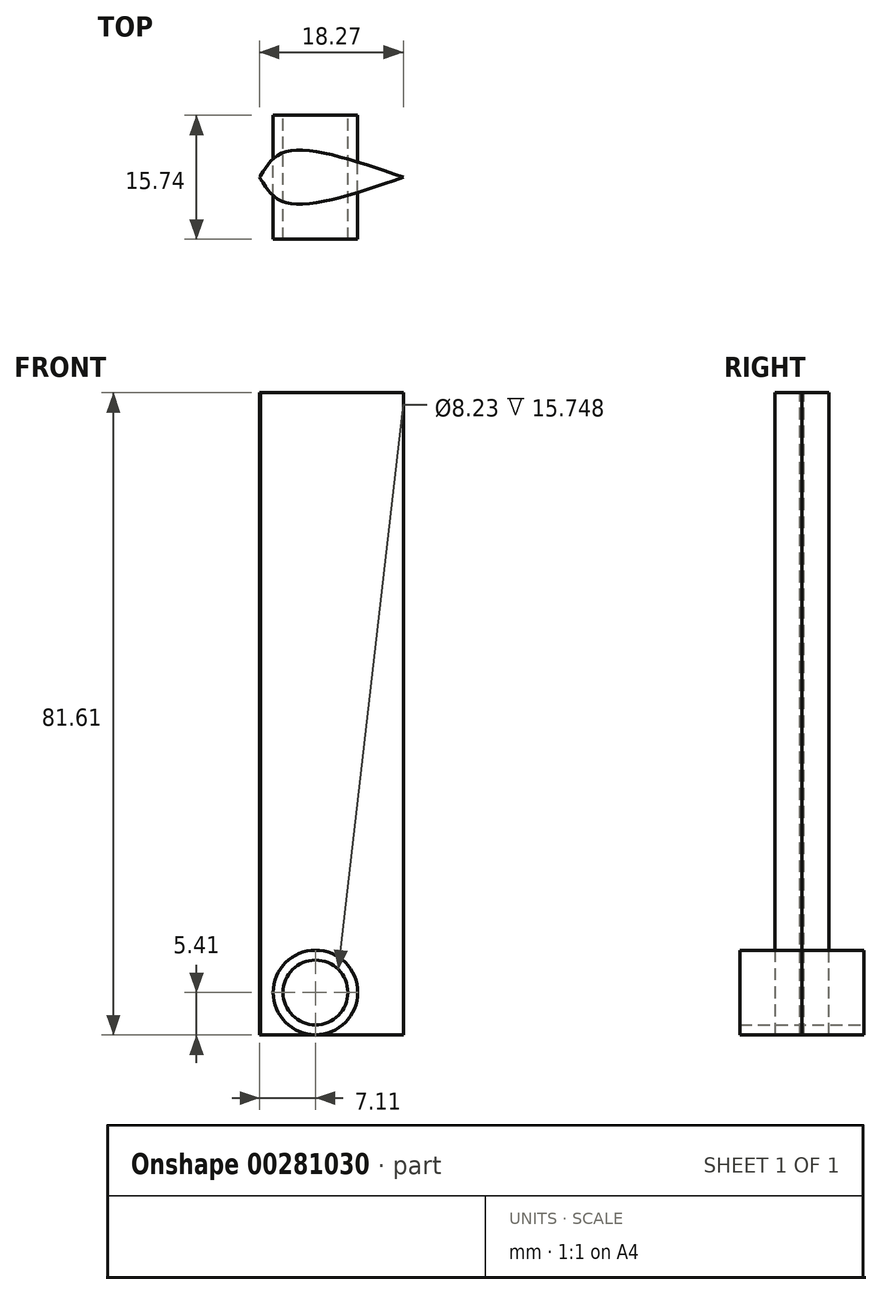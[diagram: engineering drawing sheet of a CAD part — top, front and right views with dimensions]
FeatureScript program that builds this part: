
annotation { "Feature Type Name" : "Feature", "Feature Type Description" : "" }
export const myFeature = defineFeature(function(context is Context, id is Id, definition is map)
    precondition{}
    {
        {
            var Q0;
            Q0=qCreatedBy(makeId("Top.planeOp"),FACE);
            cPlane(context, id + "F0", {"entities" : qUnion([Q0]), "cplaneType" : CPlaneType.OFFSET, "offset" : 76.2 * mm, "width" : 152.4 * mm, "height" : 152.4 * mm});
        }
        {
            var Q0;
            Q0=qCreatedBy(makeId("Front.planeOp"),FACE);
            var sketch = newSketch(context, id + "F1", { "sketchPlane" : qUnion([Q0])});
            skCircle(sketch, "E0", {"center": v(0, 0) * mm, "radius": 4.11 * mm});
            skCircle(sketch, "E1", {"center": v(0, 0) * mm, "radius": 5.37 * mm});
            skSolve(sketch);
        }
        {
            var Q0;
            Q0 = qSketchRegion(id + "F1", true);
            extrude(context, id + "F2", {"entities" : qUnion([Q0]), "depth" : 7.87 * mm, "hasSecondDirection" : true, "secondDirectionOppositeDirection" : true, "secondDirectionDepth" : 7.87 * mm});
        }
        {
            var Q0;
            Q0=qCreatedBy(id+"F0.planeOp",FACE);
            var sketch = newSketch(context, id + "F3", { "sketchPlane" : qUnion([Q0])});
            skFitSpline(sketch, "E2", {"points": [v(-6.98, -0.23) * mm, v(-3.72, -3.26) * mm, v(11.16, 0) * mm], "startDerivative": vector(6.9, -11.01) * mm, "endDerivative": vector(27.35, 9.44) * mm});
            skFitSpline(sketch, "E3.MirrorCS", {"points": [v(-6.98, 0.23) * mm, v(-3.72, 3.26) * mm, v(11.16, 0) * mm], "startDerivative": vector(6.9, 11.01) * mm, "endDerivative": vector(27.35, -9.44) * mm});
            skLineSegment(sketch, "E4", {"start": v(-6.98, -0.23) * mm, "end": v(-7.11, 0) * mm});
            skLineSegment(sketch, "E5", {"start": v(-7.11, 0) * mm, "end": v(-6.98, 0.23) * mm});
            skSolve(sketch);
        }
        {
            var Q0;
            Q0 = qSketchRegion(id + "F3", true);
            extrude(context, id + "F4", {"entities" : qUnion([Q0]), "oppositeDirection" : true, "depth" : 81.61 * mm});
        }
    });
